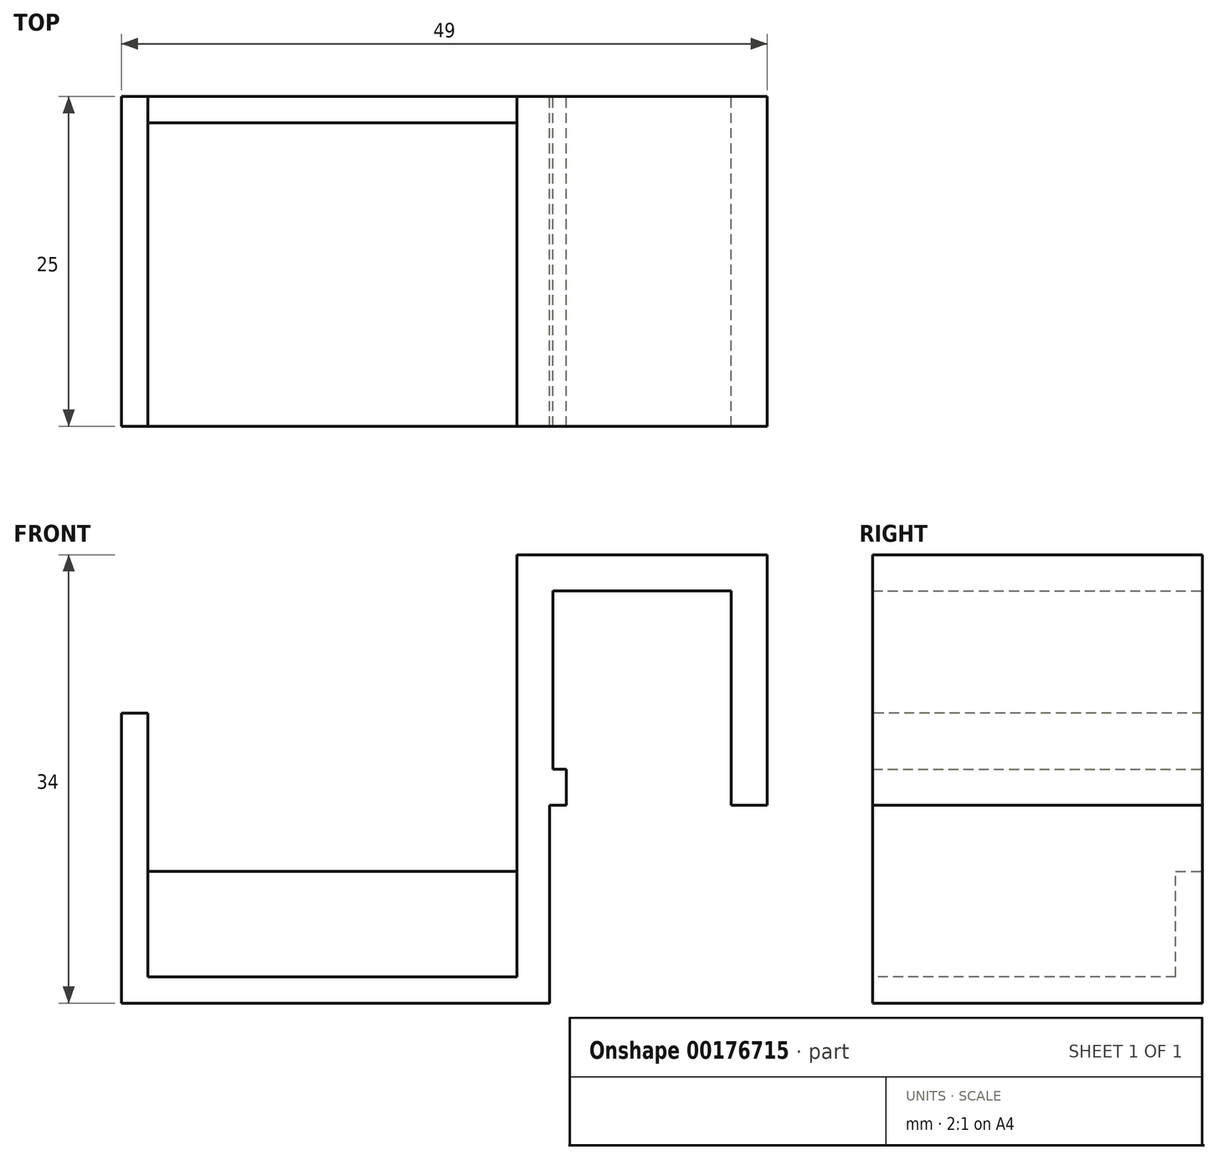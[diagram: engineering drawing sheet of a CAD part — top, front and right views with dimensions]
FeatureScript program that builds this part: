
annotation { "Feature Type Name" : "Feature", "Feature Type Description" : "" }
export const myFeature = defineFeature(function(context is Context, id is Id, definition is map)
    precondition{}
    {
        {
            var Q0;
            Q0=qCreatedBy(makeId("Front.planeOp"),FACE);
            var sketch = newSketch(context, id + "F0", { "sketchPlane" : qUnion([Q0])});
            skLineSegment(sketch, "E0.bottom", {"start": v(9.5, 9.5) * mm, "end": v(-9.5, 9.5) * mm});
            skLineSegment(sketch, "E0.top", {"start": v(9.5, -9.5) * mm, "end": v(-9.5, -9.5) * mm});
            skLineSegment(sketch, "E0.left", {"start": v(9.5, 9.5) * mm, "end": v(9.5, -9.5) * mm});
            skLineSegment(sketch, "E0.right", {"start": v(-9.5, 9.5) * mm, "end": v(-9.5, -9.5) * mm});
            skPoint(sketch, "E0.middle", {"position": v(0, 0) * mm});
            skLineSegment(sketch, "E1.bottom", {"start": v(6.75, 6.75) * mm, "end": v(-6.75, 6.75) * mm});
            skLineSegment(sketch, "E1.top", {"start": v(6.75, -6.75) * mm, "end": v(-6.75, -6.75) * mm});
            skLineSegment(sketch, "E1.left", {"start": v(6.75, 6.75) * mm, "end": v(6.75, -6.75) * mm});
            skLineSegment(sketch, "E1.right", {"start": v(-6.75, 6.75) * mm, "end": v(-6.75, -6.75) * mm});
            skLineSegment(sketch, "E2", {"start": v(-5.75, -6.75) * mm, "end": v(-5.75, -9.5) * mm});
            skLineSegment(sketch, "E3", {"start": v(-5.75, -9.5) * mm, "end": v(6.75, -9.5) * mm});
            skLineSegment(sketch, "E4", {"start": v(6.75, -9.5) * mm, "end": v(6.75, -6.75) * mm});
            skSolve(sketch);
        }
        {
            var Q0;
            Q0=makeQuery(id+"F0.imprint","IMPRINT",FACE,{"disambiguationData":[TD([[makeQuery(id+"F0.imprint","IMPRINT",EDGE,{"derivedFrom":sQuery(id+"F0.wireOp",EDGE,"E0.bottom")}),1.0]])]});
            extrude(context, id + "F1", {"entities" : qUnion([Q0]), "endBound" : BoundingType.SYMMETRIC, "depth" : 25 * mm});
        }
        {
            var Q0;
            Q0=makeQuery(id+"F1.opExtrude","SWEPT_FACE",FACE,{"disambiguationData":[OSD([sQuery(id+"F0.wireOp",EDGE,"E0.right")])]});
            var sketch = newSketch(context, id + "F2", { "sketchPlane" : qUnion([Q0])});
            skLineSegment(sketch, "E5.bottom", {"start": v(-12.5, 9.5) * mm, "end": v(12.5, 9.5) * mm});
            skLineSegment(sketch, "E5.top", {"start": v(-12.5, -24.5) * mm, "end": v(12.5, -24.5) * mm});
            skLineSegment(sketch, "E5.left", {"start": v(-12.5, 9.5) * mm, "end": v(-12.5, -24.5) * mm});
            skLineSegment(sketch, "E5.right", {"start": v(12.5, 9.5) * mm, "end": v(12.5, -24.5) * mm});
            skSolve(sketch);
        }
        {
            var Q0;
            Q0=qSketchRegion(id+"F2",true);
            extrude(context, id + "F3", {"entities" : qUnion([Q0]), "operationType" : NewBodyOperationType.ADD, "oppositeDirection" : true, "depth" : 2.5 * mm});
        }
        {
            var Q0;
            Q0=makeQuery(id+"F3.boolean.opBoolean","MERGE",FACE,{"derivedFrom":[makeQuery(id+"F1.opExtrude","SWEPT_FACE",FACE,{"disambiguationData":[OSD([sQuery(id+"F0.wireOp",EDGE,"E0.right")])]}),makeQuery(id+"F3.opExtrude","CAP_FACE",FACE,{"disambiguationData":[OSD([sQuery(id+"F2.wireOp",EDGE,"E5.bottom"),sQuery(id+"F2.wireOp",EDGE,"E5.top"),sQuery(id+"F2.wireOp",EDGE,"E5.left"),sQuery(id+"F2.wireOp",EDGE,"E5.right")])],"isStart":true})]});
            var sketch = newSketch(context, id + "F4", { "sketchPlane" : qUnion([Q0])});
            skLineSegment(sketch, "E6.bottom", {"start": v(-12.5, -24.5) * mm, "end": v(12.5, -24.5) * mm});
            skLineSegment(sketch, "E6.top", {"start": v(-12.5, -22.5) * mm, "end": v(12.5, -22.5) * mm});
            skLineSegment(sketch, "E6.left", {"start": v(-12.5, -24.5) * mm, "end": v(-12.5, -22.5) * mm});
            skLineSegment(sketch, "E6.right", {"start": v(12.5, -24.5) * mm, "end": v(12.5, -22.5) * mm});
            skSolve(sketch);
        }
        {
            var Q0;
            Q0=qSketchRegion(id+"F4",true);
            extrude(context, id + "F5", {"entities" : qUnion([Q0]), "operationType" : NewBodyOperationType.ADD, "depth" : 30 * mm});
        }
        {
            var Q0;
            Q0=makeQuery(id+"F5.opExtrude","SWEPT_FACE",FACE,{"disambiguationData":[OSD([sQuery(id+"F4.wireOp",EDGE,"E6.top")])]});
            var sketch = newSketch(context, id + "F6", { "sketchPlane" : qUnion([Q0])});
            skLineSegment(sketch, "E7.bottom", {"start": v(-39.5, 12.5) * mm, "end": v(-37.5, 12.5) * mm});
            skLineSegment(sketch, "E7.top", {"start": v(-39.5, -12.5) * mm, "end": v(-37.5, -12.5) * mm});
            skLineSegment(sketch, "E7.left", {"start": v(-39.5, 12.5) * mm, "end": v(-39.5, -12.5) * mm});
            skLineSegment(sketch, "E7.right", {"start": v(-37.5, 12.5) * mm, "end": v(-37.5, -12.5) * mm});
            skSolve(sketch);
        }
        {
            var Q0;
            Q0=qSketchRegion(id+"F6",true);
            extrude(context, id + "F7", {"entities" : qUnion([Q0]), "operationType" : NewBodyOperationType.ADD, "depth" : 20 * mm});
        }
        {
            var Q0;
            Q0=makeQuery(id+"F7.boolean.opBoolean","MERGE",FACE,{"derivedFrom":[makeQuery(id+"F5.boolean.opBoolean","MERGE",FACE,{"derivedFrom":[makeQuery(id+"F3.boolean.opBoolean","MERGE",FACE,{"derivedFrom":[makeQuery(id+"F1.opExtrude","CAP_FACE",FACE,{"disambiguationData":[OSD([sQuery(id+"F0.wireOp",EDGE,"E0.bottom"),sQuery(id+"F0.wireOp",EDGE,"E0.top"),sQuery(id+"F0.wireOp",EDGE,"E0.left"),sQuery(id+"F0.wireOp",EDGE,"E0.right"),sQuery(id+"F0.wireOp",EDGE,"E1.bottom"),sQuery(id+"F0.wireOp",EDGE,"E1.top"),sQuery(id+"F0.wireOp",EDGE,"E1.left"),sQuery(id+"F0.wireOp",EDGE,"E1.right")])],"isStart":true}),makeQuery(id+"F3.opExtrude","SWEPT_FACE",FACE,{"disambiguationData":[OSD([sQuery(id+"F2.wireOp",EDGE,"E5.left")])]})]}),makeQuery(id+"F5.opExtrude","SWEPT_FACE",FACE,{"disambiguationData":[OSD([sQuery(id+"F4.wireOp",EDGE,"E6.left")])]})]}),makeQuery(id+"F7.opExtrude","SWEPT_FACE",FACE,{"disambiguationData":[OSD([sQuery(id+"F6.wireOp",EDGE,"E7.bottom")])]})]});
            var sketch = newSketch(context, id + "F8", { "sketchPlane" : qUnion([Q0])});
            skLineSegment(sketch, "E8.bottom", {"start": v(7, -24.5) * mm, "end": v(39.5, -24.5) * mm});
            skLineSegment(sketch, "E8.top", {"start": v(7, -14.5) * mm, "end": v(39.5, -14.5) * mm});
            skLineSegment(sketch, "E8.left", {"start": v(7, -24.5) * mm, "end": v(7, -14.5) * mm});
            skLineSegment(sketch, "E8.right", {"start": v(39.5, -24.5) * mm, "end": v(39.5, -14.5) * mm});
            skSolve(sketch);
        }
        {
            var Q0;
            Q0=qSketchRegion(id+"F8",true);
            extrude(context, id + "F9", {"entities" : qUnion([Q0]), "operationType" : NewBodyOperationType.ADD, "oppositeDirection" : true, "depth" : 2 * mm});
        }
    });
